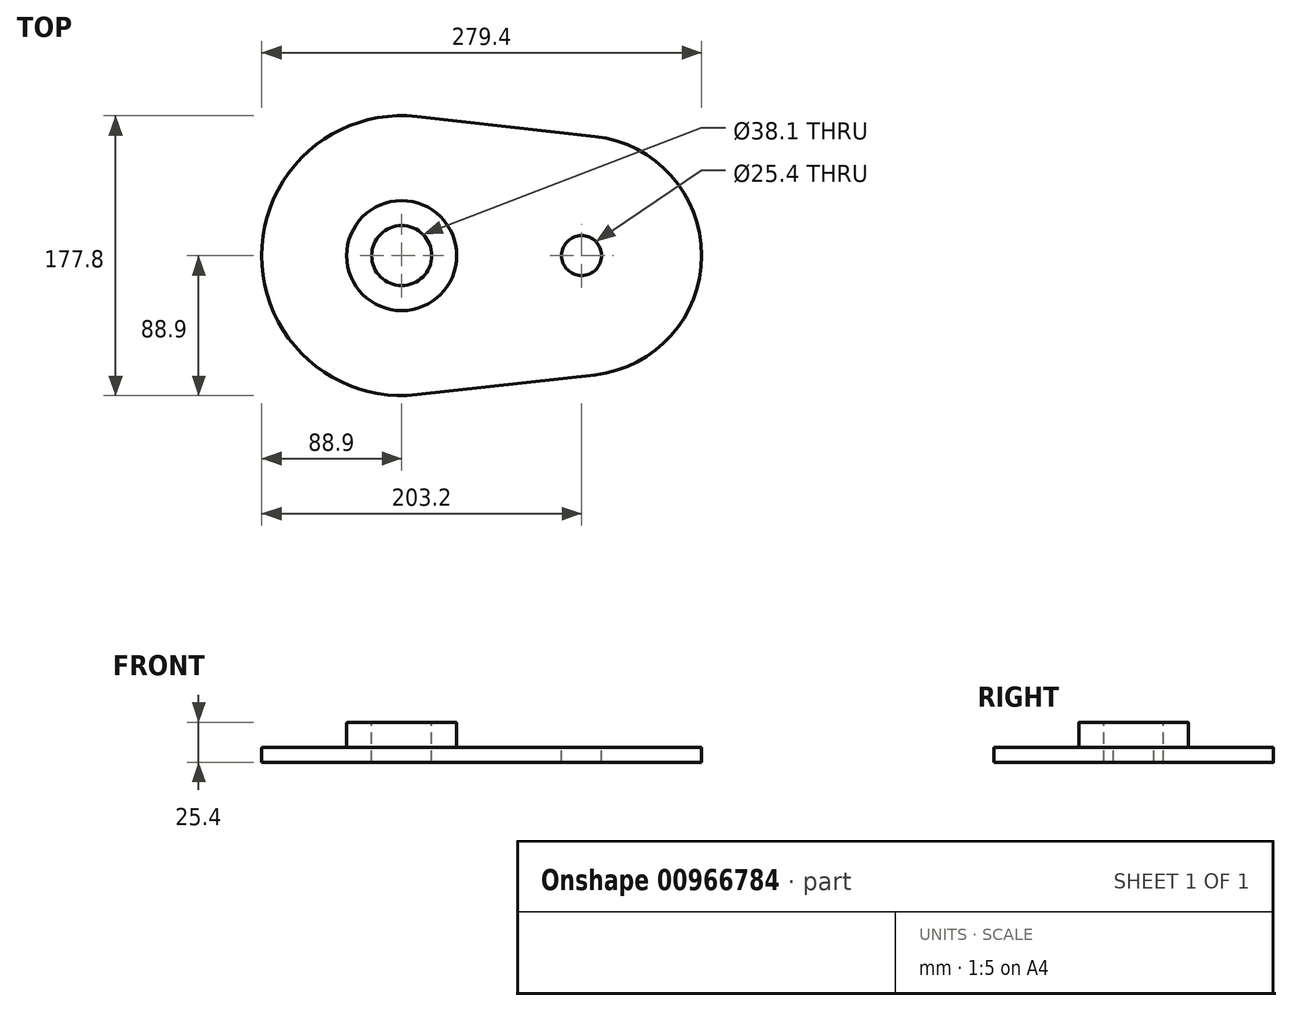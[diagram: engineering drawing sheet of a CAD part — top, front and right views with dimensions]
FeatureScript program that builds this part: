
annotation { "Feature Type Name" : "Feature", "Feature Type Description" : "" }
export const myFeature = defineFeature(function(context is Context, id is Id, definition is map)
    precondition{}
    {
        {
            var Q0;
            Q0=qCreatedBy(makeId("Top.planeOp"),FACE);
            var sketch = newSketch(context, id + "F0", { "sketchPlane" : qUnion([Q0])});
            skArc(sketch, "E0", {"start": v(9.88, 88.35) * mm, "mid": v(-88.9, 0) * mm, "end": v(9.88, -88.35) * mm});
            skArc(sketch, "E1", {"start": v(122.77, -75.73) * mm, "mid": v(190.5, 0) * mm, "end": v(122.77, 75.73) * mm});
            skLineSegment(sketch, "E2", {"start": v(9.88, 88.35) * mm, "end": v(122.77, 75.73) * mm});
            skLineSegment(sketch, "E3", {"start": v(9.88, -88.35) * mm, "end": v(122.77, -75.73) * mm});
            skLineSegment(sketch, "E4", {"start": v(0, 0) * mm, "end": v(224.72, 0) * mm, "construction": true});
            skPoint(sketch, "E4.endSnap0", {"position": v(190.5, 0) * mm});
            skSolve(sketch);
        }
        {
            var Q0;
            Q0=makeQuery(id+"F0.imprint","IMPRINT",FACE,{"disambiguationData":[TD([[makeQuery(id+"F0.imprint","IMPRINT",EDGE,{"derivedFrom":sQuery(id+"F0.wireOp",EDGE,"E0")}),1.0]])]});
            extrude(context, id + "F1", {"entities" : qUnion([Q0]), "depth" : 9.52 * mm});
        }
        {
            var Q0;
            Q0=makeQuery(id+"F1.opExtrude","CAP_FACE",FACE,{"disambiguationData":[OSD([sQuery(id+"F0.wireOp",EDGE,"E0"),sQuery(id+"F0.wireOp",EDGE,"E1"),sQuery(id+"F0.wireOp",EDGE,"E2"),sQuery(id+"F0.wireOp",EDGE,"E3")])],"isStart":false});
            var sketch = newSketch(context, id + "F2", { "sketchPlane" : qUnion([Q0])});
            skCircle(sketch, "E5", {"center": v(0, 0) * mm, "radius": 34.93 * mm});
            skSolve(sketch);
        }
        {
            var Q0;
            Q0=qSketchRegion(id+"F2",true);
            var Q1;
            Q1=makeQuery(id+"F2.imprint","IMPRINT",FACE,{"disambiguationData":[TD([[makeQuery(id+"F2.imprint","IMPRINT",EDGE,{"derivedFrom":sQuery(id+"F2.wireOp",EDGE,"E5")}),1.0]])]});
            extrude(context, id + "F3", {"entities" : qUnion([Q0, Q1]), "operationType" : NewBodyOperationType.ADD, "depth" : 15.88 * mm});
        }
        {
            var Q0;
            Q0=makeQuery(id+"F3.opExtrude","CAP_FACE",FACE,{"disambiguationData":[OSD([sQuery(id+"F2.wireOp",EDGE,"E5")])],"isStart":false});
            var sketch = newSketch(context, id + "F4", { "sketchPlane" : qUnion([Q0])});
            skCircle(sketch, "E6", {"center": v(0, 0) * mm, "radius": 19.05 * mm});
            skCircle(sketch, "E7", {"center": v(114.3, 0) * mm, "radius": 12.7 * mm});
            skSolve(sketch);
        }
        {
            var Q0;
            Q0=makeQuery(id+"F4.imprint","IMPRINT",FACE,{"disambiguationData":[TD([[makeQuery(id+"F4.imprint","IMPRINT",EDGE,{"derivedFrom":sQuery(id+"F4.wireOp",EDGE,"E6")}),1.0]])]});
            var Q1;
            Q1=makeQuery(id+"F4.imprint","IMPRINT",FACE,{"disambiguationData":[TD([[makeQuery(id+"F4.imprint","IMPRINT",EDGE,{"derivedFrom":sQuery(id+"F4.wireOp",EDGE,"E7")}),1.0]])]});
            extrude(context, id + "F5", {"entities" : qUnion([Q0, Q1]), "operationType" : NewBodyOperationType.REMOVE, "endBound" : BoundingType.THROUGH_ALL, "oppositeDirection" : true, "depth" : 25.4 * mm});
        }
        {
            var Q0;
            Q0=makeQuery(id+"F3.opExtrude","CAP_EDGE",EDGE,{"disambiguationData":[OSD([sQuery(id+"F2.wireOp",EDGE,"E5")])],"isStart":true});
            var Q1;
            Q1=makeQuery(id+"F3.opExtrude","CAP_EDGE",EDGE,{"disambiguationData":[OSD([sQuery(id+"F2.wireOp",EDGE,"E5")])],"isStart":false});
            var Q2;
            Q2=makeQuery(id+"F1.opExtrude","CAP_EDGE",EDGE,{"disambiguationData":[OSD([sQuery(id+"F0.wireOp",EDGE,"E1")])],"isStart":false});
            var Q3;
            Q3=makeQuery(id+"F1.opExtrude","CAP_EDGE",EDGE,{"disambiguationData":[OSD([sQuery(id+"F0.wireOp",EDGE,"E3")])],"isStart":false});
            var Q4;
            Q4=makeQuery(id+"F1.opExtrude","CAP_FACE",FACE,{"disambiguationData":[OSD([sQuery(id+"F0.wireOp",EDGE,"E0"),sQuery(id+"F0.wireOp",EDGE,"E1"),sQuery(id+"F0.wireOp",EDGE,"E2"),sQuery(id+"F0.wireOp",EDGE,"E3")])],"isStart":false});
            fillet(context, id + "F6", {"entities" : qUnion([Q0, Q1, Q2, Q3, Q4]), "radius" : 0.8 * mm, "tangentPropagation" : true, "allowEdgeOverflow" : false});
        }
    });
